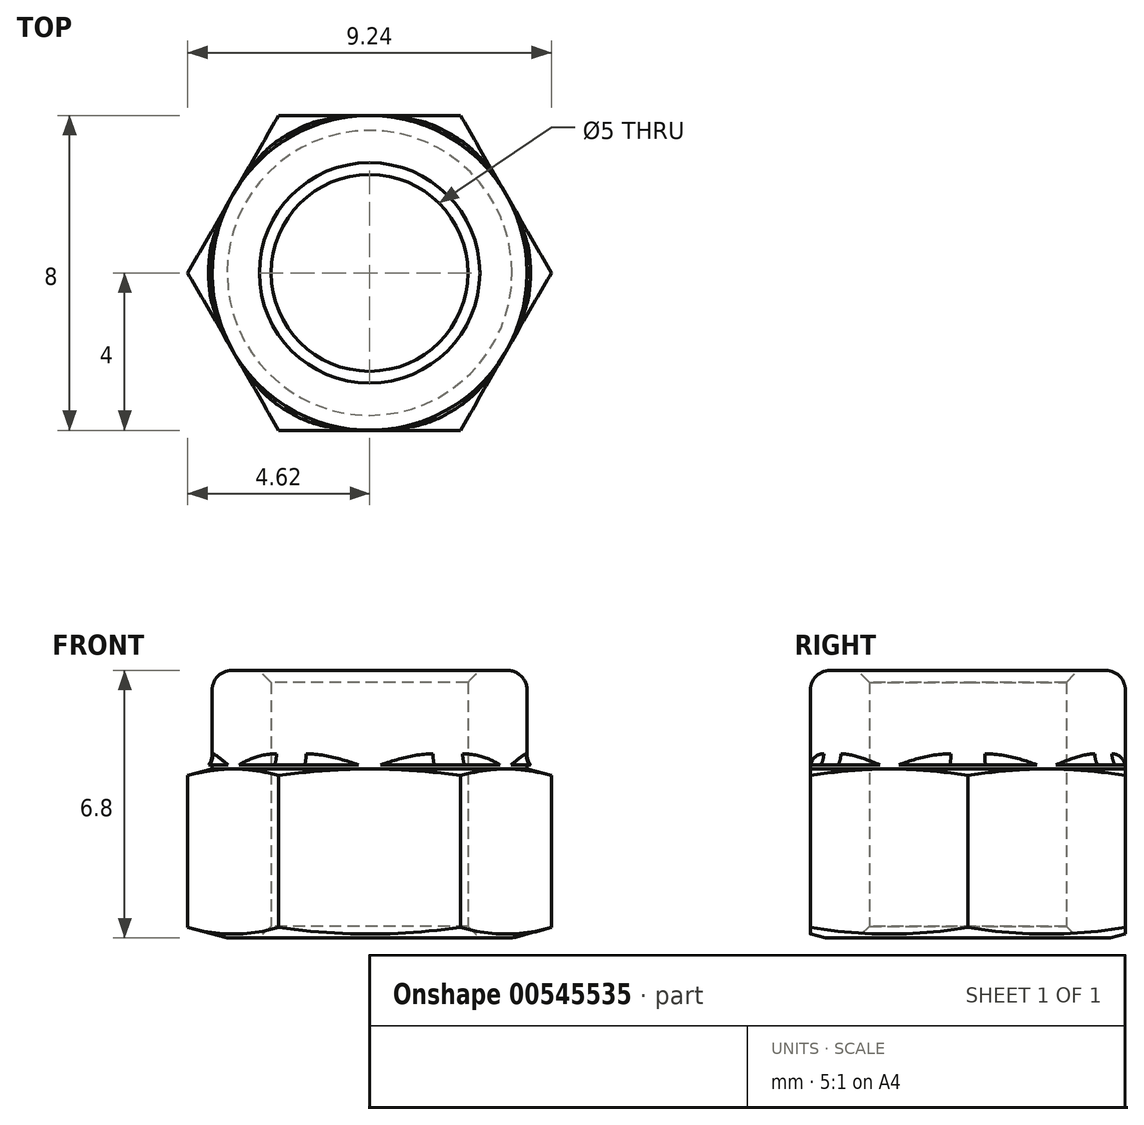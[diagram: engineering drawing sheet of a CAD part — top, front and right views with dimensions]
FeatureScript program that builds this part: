
annotation { "Feature Type Name" : "Feature", "Feature Type Description" : "" }
export const myFeature = defineFeature(function(context is Context, id is Id, definition is map)
    precondition{}
    {
        {
            var Q0;
            Q0=qCreatedBy(makeId("Top.planeOp"),FACE);
            var sketch = newSketch(context, id + "F0", { "sketchPlane" : qUnion([Q0])});
            skCircle(sketch, "E0.cCircle", {"center": v(0, 0) * mm, "radius": 4 * mm, "construction": true});
            skLineSegment(sketch, "E0.0", {"start": v(-2.3, 4) * mm, "end": v(2.3, 4) * mm});
            skLineSegment(sketch, "E0.1", {"start": v(2.3, 4) * mm, "end": v(4.62, 0) * mm});
            skLineSegment(sketch, "E0.2", {"start": v(4.62, 0) * mm, "end": v(2.3, -4) * mm});
            skLineSegment(sketch, "E0.3", {"start": v(2.3, -4) * mm, "end": v(-2.3, -4) * mm});
            skLineSegment(sketch, "E0.4", {"start": v(-2.3, -4) * mm, "end": v(-4.62, 0) * mm});
            skLineSegment(sketch, "E0.5", {"start": v(-4.62, 0) * mm, "end": v(-2.3, 4) * mm});
            skPoint(sketch, "E0.0.midPoint", {"position": v(0, 4) * mm});
            skCircle(sketch, "E1", {"center": v(0, 0) * mm, "radius": 2.5 * mm});
            skCircle(sketch, "E2", {"center": v(0, 0) * mm, "radius": 4 * mm});
            skSolve(sketch);
        }
        {
            var Q0;
            Q0=makeQuery(id+"F0.imprint","IMPRINT",FACE,{"disambiguationData":[TD([[makeQuery(id+"F0.imprint","IMPRINT",EDGE,{"derivedFrom":sQuery(id+"F0.wireOp",EDGE,"E1")}),-1.0]])]});
            var Q1;
            {var subQ0=sQuery(id+"F0.wireOp",EDGE,"E0.5");var subQ1=sQuery(id+"F0.wireOp",EDGE,"E0.4");var subQ2=makeQuery(id+"F0.imprint","INTERSECT",VERTEX,{"derivedFrom":[subQ1,subQ0]});Q1=makeQuery(id+"F0.imprint","IMPRINT",FACE,{"disambiguationData":[TD([[makeQuery(id+"F0.imprint","IMPRINT",EDGE,{"disambiguationData":[TD([[subQ2,1.0]])],"derivedFrom":subQ1}),-1.0]])]});}
            var Q2;
            {var subQ0=sQuery(id+"F0.wireOp",EDGE,"E0.5");var subQ1=sQuery(id+"F0.wireOp",EDGE,"E0.0");var subQ2=makeQuery(id+"F0.imprint","INTERSECT",VERTEX,{"derivedFrom":[subQ1,subQ0]});Q2=makeQuery(id+"F0.imprint","IMPRINT",FACE,{"disambiguationData":[TD([[makeQuery(id+"F0.imprint","IMPRINT",EDGE,{"disambiguationData":[TD([[subQ2,-1.0]])],"derivedFrom":subQ1}),-1.0]])]});}
            var Q3;
            {var subQ0=sQuery(id+"F0.wireOp",EDGE,"E0.1");var subQ1=sQuery(id+"F0.wireOp",EDGE,"E0.0");var subQ2=makeQuery(id+"F0.imprint","INTERSECT",VERTEX,{"derivedFrom":[subQ1,subQ0]});Q3=makeQuery(id+"F0.imprint","IMPRINT",FACE,{"disambiguationData":[TD([[makeQuery(id+"F0.imprint","IMPRINT",EDGE,{"disambiguationData":[TD([[subQ2,1.0]])],"derivedFrom":subQ1}),-1.0]])]});}
            var Q4;
            {var subQ0=sQuery(id+"F0.wireOp",EDGE,"E0.2");var subQ1=sQuery(id+"F0.wireOp",EDGE,"E0.1");var subQ2=makeQuery(id+"F0.imprint","INTERSECT",VERTEX,{"derivedFrom":[subQ1,subQ0]});Q4=makeQuery(id+"F0.imprint","IMPRINT",FACE,{"disambiguationData":[TD([[makeQuery(id+"F0.imprint","IMPRINT",EDGE,{"disambiguationData":[TD([[subQ2,1.0]])],"derivedFrom":subQ1}),-1.0]])]});}
            var Q5;
            {var subQ0=sQuery(id+"F0.wireOp",EDGE,"E0.3");var subQ1=sQuery(id+"F0.wireOp",EDGE,"E0.2");var subQ2=makeQuery(id+"F0.imprint","INTERSECT",VERTEX,{"derivedFrom":[subQ1,subQ0]});Q5=makeQuery(id+"F0.imprint","IMPRINT",FACE,{"disambiguationData":[TD([[makeQuery(id+"F0.imprint","IMPRINT",EDGE,{"disambiguationData":[TD([[subQ2,1.0]])],"derivedFrom":subQ1}),-1.0]])]});}
            var Q6;
            {var subQ0=sQuery(id+"F0.wireOp",EDGE,"E0.4");var subQ1=sQuery(id+"F0.wireOp",EDGE,"E0.3");var subQ2=makeQuery(id+"F0.imprint","INTERSECT",VERTEX,{"derivedFrom":[subQ1,subQ0]});Q6=makeQuery(id+"F0.imprint","IMPRINT",FACE,{"disambiguationData":[TD([[makeQuery(id+"F0.imprint","IMPRINT",EDGE,{"disambiguationData":[TD([[subQ2,1.0]])],"derivedFrom":subQ1}),-1.0]])]});}
            extrude(context, id + "F1", {"entities" : qUnion([Q0, Q1, Q2, Q3, Q4, Q5, Q6]), "depth" : 4.4 * mm, "offsetDistance" : 25 * mm});
        }
        {
            var Q0;
            Q0=qCreatedBy(makeId("Front.planeOp"),FACE);
            var sketch = newSketch(context, id + "F2", { "sketchPlane" : qUnion([Q0])});
            skPoint(sketch, "E3.0", {"position": v(-4.62, 4.4) * mm});
            skLineSegment(sketch, "E4", {"start": v(-4.62, 4.4) * mm, "end": v(-3.62, 4.4) * mm});
            skLineSegment(sketch, "E5", {"start": v(-3.62, 4.4) * mm, "end": v(-4.62, 4.13) * mm});
            skLineSegment(sketch, "E6", {"start": v(-4.62, 4.13) * mm, "end": v(-4.62, 4.4) * mm});
            skPoint(sketch, "E7.0", {"position": v(-4.62, 2.2) * mm});
            skLineSegment(sketch, "E8", {"start": v(-4.62, 2.2) * mm, "end": v(-5.62, 2.2) * mm, "construction": true});
            skLineSegment(sketch, "E9.MirrorCS", {"start": v(-3.62, 0) * mm, "end": v(-4.62, 0.27) * mm});
            skLineSegment(sketch, "E10.MirrorCS", {"start": v(-4.62, 0) * mm, "end": v(-3.62, 0) * mm});
            skLineSegment(sketch, "E11.MirrorCS", {"start": v(-4.62, 0.27) * mm, "end": v(-4.62, 0) * mm});
            skPoint(sketch, "E12.0", {"position": v(0, 4.4) * mm});
            skLineSegment(sketch, "E13", {"start": v(0, 4.4) * mm, "end": v(0, 5.4) * mm, "construction": true});
            skSolve(sketch);
        }
        {
            var Q0;
            Q0=makeQuery(id+"F2.imprint","IMPRINT",FACE,{"disambiguationData":[TD([[makeQuery(id+"F2.imprint","IMPRINT",EDGE,{"derivedFrom":sQuery(id+"F2.wireOp",EDGE,"E4")}),-1.0]])]});
            var Q1;
            Q1=makeQuery(id+"F2.imprint","IMPRINT",FACE,{"disambiguationData":[TD([[makeQuery(id+"F2.imprint","IMPRINT",EDGE,{"derivedFrom":sQuery(id+"F2.wireOp",EDGE,"E9.MirrorCS")}),1.0]])]});
            var Q2;
            Q2=sQuery(id+"F2.wireOp",EDGE,"E13");
            revolve(context, id + "F3", {"operationType" : NewBodyOperationType.REMOVE, "entities" : qUnion([Q0, Q1]), "axis" : qUnion([Q2]), "revolveType" : RevolveType.FULL, "oppositeDirection" : true});
        }
        {
            var Q0;
            Q0=makeQuery(id+"F0.imprint","IMPRINT",FACE,{"disambiguationData":[TD([[makeQuery(id+"F0.imprint","IMPRINT",EDGE,{"derivedFrom":sQuery(id+"F0.wireOp",EDGE,"E1")}),-1.0]])]});
            extrude(context, id + "F4", {"entities" : qUnion([Q0]), "operationType" : NewBodyOperationType.ADD, "depth" : 6.8 * mm, "offsetDistance" : 25 * mm, "hasSecondDirection" : true, "secondDirectionOppositeDirection" : false, "secondDirectionDepth" : 2 * mm});
        }
        {
            var Q0;
            Q0=makeQuery(id+"F4.opExtrude","CAP_EDGE",EDGE,{"disambiguationData":[OSD([sQuery(id+"F0.wireOp",EDGE,"E2")])],"isStart":false});
            var Q1;
            Q1=makeQuery(id+"F4.boolean.opBoolean","INTERSECT",EDGE,{"disambiguationData":[OD(4.0)],"derivedFrom":[makeQuery(id+"F3.boolean.opBoolean","COPY",FACE,{"derivedFrom":makeQuery(id+"F3.opRevolve","SWEPT_FACE",FACE,{"disambiguationData":[OSD([sQuery(id+"F2.wireOp",EDGE,"E5")])]})}),makeQuery(id+"F4.opExtrude","SWEPT_FACE",FACE,{"disambiguationData":[OSD([sQuery(id+"F0.wireOp",EDGE,"E2")])]})]});
            fillet(context, id + "F5", {"entities" : qUnion([Q0, Q1]), "radius" : .5 * mm, "tangentPropagation" : true, "allowEdgeOverflow" : false});
        }
        {
            var Q0;
            Q0=makeQuery(id+"F1.opExtrude","CAP_EDGE",EDGE,{"disambiguationData":[OSD([sQuery(id+"F0.wireOp",EDGE,"E1")])],"isStart":true});
            var Q1;
            Q1=makeQuery(id+"F4.opExtrude","CAP_EDGE",EDGE,{"disambiguationData":[OSD([sQuery(id+"F0.wireOp",EDGE,"E1")])],"isStart":false});
            chamfer(context, id + "F6", {"entities" : qUnion([Q0, Q1]), "width" : .3 * mm, "tangentPropagation" : true});
        }
    });
